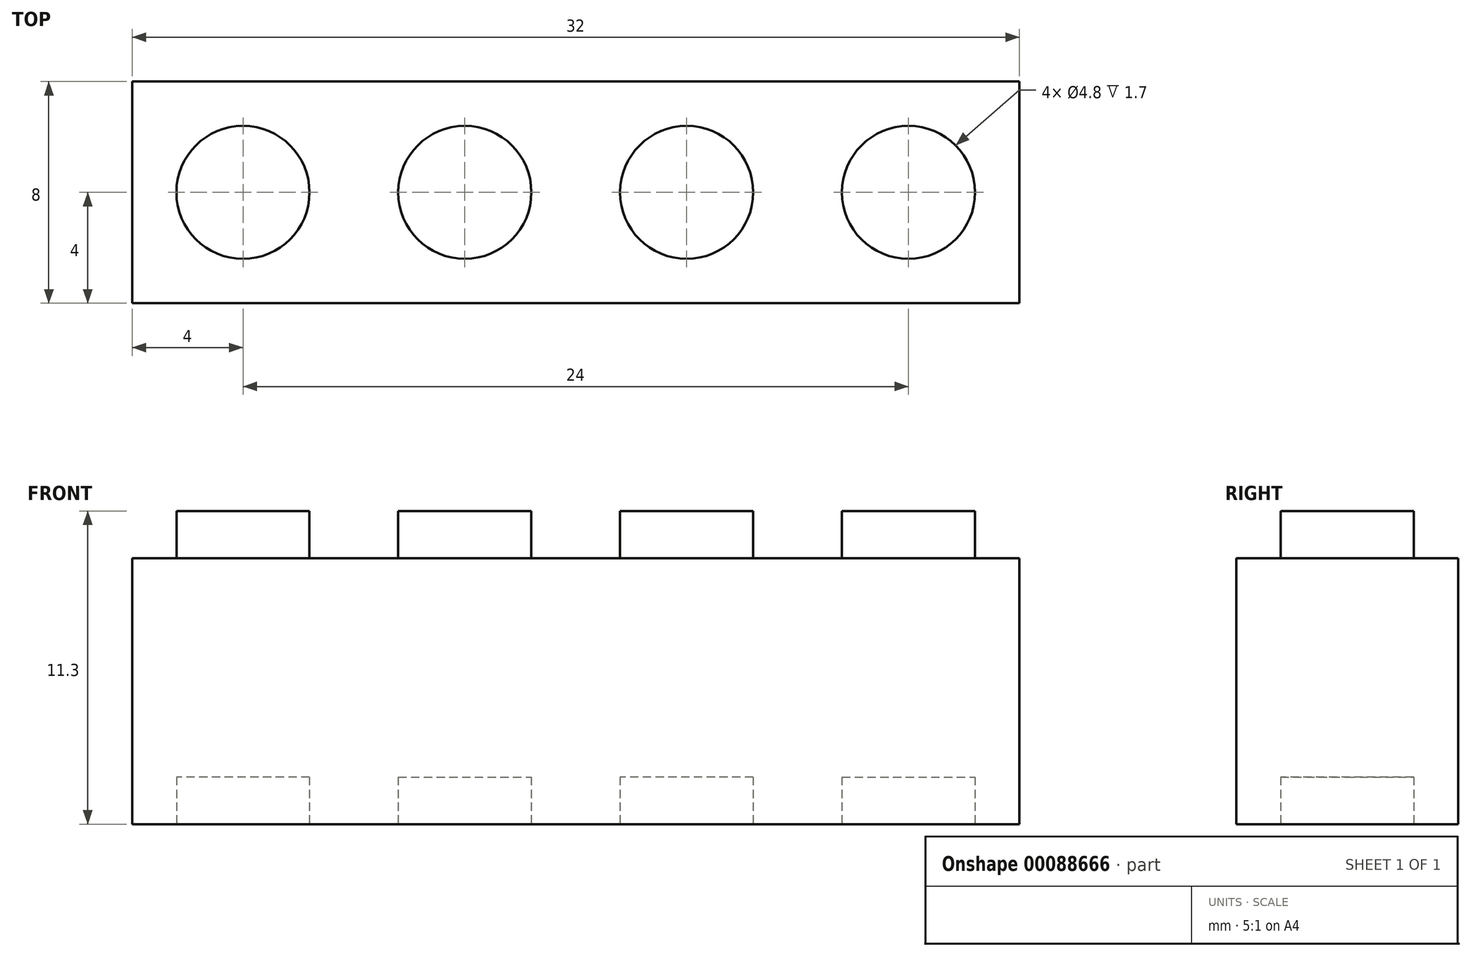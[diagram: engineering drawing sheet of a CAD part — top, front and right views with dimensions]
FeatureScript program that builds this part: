
annotation { "Feature Type Name" : "Feature", "Feature Type Description" : "" }
export const myFeature = defineFeature(function(context is Context, id is Id, definition is map)
    precondition{}
    {
        {
            var Q0;
            Q0=qCreatedBy(makeId("Front.planeOp"),FACE);
            var sketch = newSketch(context, id + "F0", { "sketchPlane" : qUnion([Q0])});
            skLineSegment(sketch, "E0.bottom", {"start": v(-4, 9.6) * mm, "end": v(-2.4, 9.6) * mm});
            skLineSegment(sketch, "E0.top", {"start": v(-4, 0) * mm, "end": v(4, 0) * mm});
            skLineSegment(sketch, "E0.left", {"start": v(-4, 9.6) * mm, "end": v(-4, 0) * mm});
            skLineSegment(sketch, "E0.right", {"start": v(4, 9.6) * mm, "end": v(4, 0) * mm});
            skLineSegment(sketch, "E1.top", {"start": v(-2.4, 11.3) * mm, "end": v(2.4, 11.3) * mm});
            skLineSegment(sketch, "E1.left", {"start": v(-2.4, 9.6) * mm, "end": v(-2.4, 11.3) * mm});
            skLineSegment(sketch, "E1.right", {"start": v(2.4, 9.6) * mm, "end": v(2.4, 11.3) * mm});
            skLineSegment(sketch, "E2", {"start": v(0, 0) * mm, "end": v(0, 24.04) * mm, "construction": true});
            skLineSegment(sketch, "E3.trimOffspring", {"start": v(2.4, 9.6) * mm, "end": v(4, 9.6) * mm});
            skSolve(sketch);
        }
        {
            var Q0;
            Q0=makeQuery(id+"F0.imprint","IMPRINT",FACE,{"disambiguationData":[TD([[makeQuery(id+"F0.imprint","IMPRINT",EDGE,{"derivedFrom":sQuery(id+"F0.wireOp",EDGE,"E0.bottom")}),-1.0]])]});
            extrude(context, id + "F1", {"entities" : qUnion([Q0]), "depth" : 8 * mm});
        }
        {
            var Q0;
            Q0=qCreatedBy(makeId("Top.planeOp"),FACE);
            var Q1;
            Q1=makeQuery(id+"F1.opExtrude","CAP_VERTEX",VERTEX,{"disambiguationData":[OSD([sQuery(id+"F0.wireOp",EDGE,"E1.top"),sQuery(id+"F0.wireOp",EDGE,"E1.right")])],"isStart":true});
            cPlane(context, id + "F2", {"entities" : qUnion([Q0, Q1]), "cplaneType" : CPlaneType.PLANE_POINT, "offset" : 152.4 * mm, "width" : 152.4 * mm, "height" : 152.4 * mm});
        }
        {
            var Q0;
            Q0=qCreatedBy(id+"F2.planeOp",FACE);
            var sketch = newSketch(context, id + "F3", { "sketchPlane" : qUnion([Q0])});
            skLineSegment(sketch, "E4.0", {"start": v(-4, -8) * mm, "end": v(-4, 0) * mm});
            skLineSegment(sketch, "E5.0", {"start": v(4, -8) * mm, "end": v(4, 0) * mm});
            skLineSegment(sketch, "E6", {"start": v(-4, 0) * mm, "end": v(4, 0) * mm});
            skLineSegment(sketch, "E7", {"start": v(-4, -8) * mm, "end": v(4, -8) * mm});
            skLineSegment(sketch, "E8", {"start": v(-4, 0) * mm, "end": v(4, -8) * mm, "construction": true});
            skLineSegment(sketch, "E9", {"start": v(-4, -8) * mm, "end": v(4, 0) * mm, "construction": true});
            skCircle(sketch, "E10", {"center": v(0, -4) * mm, "radius": 2.4 * mm});
            skSolve(sketch);
        }
        {
            var Q0;
            Q0=qSketchRegion(id+"F3",true);
            var Q1;
            Q1=makeQuery(id+"F1.opExtrude","SWEPT_FACE",FACE,{"disambiguationData":[OSD([sQuery(id+"F0.wireOp",EDGE,"E0.bottom")])]});
            extrude(context, id + "F4", {"entities" : qUnion([Q0]), "operationType" : NewBodyOperationType.REMOVE, "endBound" : BoundingType.UP_TO_SURFACE, "oppositeDirection" : true, "endBoundEntityFace" : qUnion([Q1]), "depth" : 25.4 * mm});
        }
        {
            var Q0;
            Q0=qCreatedBy(makeId("Top.planeOp"),FACE);
            var sketch = newSketch(context, id + "F5", { "sketchPlane" : qUnion([Q0])});
            skCircle(sketch, "E11.0", {"center": v(0, -4) * mm, "radius": 2.4 * mm});
            skSolve(sketch);
        }
        {
            var Q0;
            Q0=makeQuery(id+"F5.imprint","IMPRINT",FACE,{"disambiguationData":[TD([[makeQuery(id+"F5.imprint","IMPRINT",EDGE,{"derivedFrom":sQuery(id+"F5.wireOp",EDGE,"E11.0")}),1.0]])]});
            extrude(context, id + "F6", {"entities" : qUnion([Q0]), "operationType" : NewBodyOperationType.REMOVE, "depth" : 1.7 * mm});
        }
        {
            var Q0;
            Q0=qCreatedBy(makeId("Right.planeOp"),FACE);
            var Q1;
            Q1=makeQuery(id+"F1.opExtrude","CAP_VERTEX",VERTEX,{"disambiguationData":[OSD([sQuery(id+"F0.wireOp",EDGE,"E0.right"),sQuery(id+"F0.wireOp",EDGE,"E3.trimOffspring")])],"isStart":false});
            cPlane(context, id + "F7", {"entities" : qUnion([Q0, Q1]), "cplaneType" : CPlaneType.PLANE_POINT, "offset" : 152.4 * mm, "width" : 152.4 * mm, "height" : 152.4 * mm});
        }
        {
            var Q0;
            Q0=makeQuery(id+"F1.opExtrude","SWEPT_BODY",BODY,{"disambiguationData":[OSD([sQuery(id+"F0.wireOp",EDGE,"E0.bottom"),sQuery(id+"F0.wireOp",EDGE,"E0.top"),sQuery(id+"F0.wireOp",EDGE,"E0.left"),sQuery(id+"F0.wireOp",EDGE,"E0.right"),sQuery(id+"F0.wireOp",EDGE,"E1.top"),sQuery(id+"F0.wireOp",EDGE,"E1.left"),sQuery(id+"F0.wireOp",EDGE,"E1.right"),sQuery(id+"F0.wireOp",EDGE,"E3.trimOffspring")])]});
            var Q1;
            Q1=qCreatedBy(id+"F7.planeOp",FACE);
            mirror(context, id + "F8", {"operationType" : NewBodyOperationType.ADD, "entities" : qUnion([Q0]), "mirrorPlane" : qUnion([Q1])});
        }
        {
            var Q0;
            Q0=qCreatedBy(id+"F7.planeOp",FACE);
            var Q1;
            Q1=makeQuery(id+"F8.opPattern","COPY",VERTEX,{"derivedFrom":makeQuery(id+"F1.opExtrude","CAP_VERTEX",VERTEX,{"disambiguationData":[OSD([sQuery(id+"F0.wireOp",EDGE,"E0.bottom"),sQuery(id+"F0.wireOp",EDGE,"E0.left")])],"isStart":false}),"instanceName":"1"});
            cPlane(context, id + "F9", {"entities" : qUnion([Q0, Q1]), "cplaneType" : CPlaneType.PLANE_POINT, "offset" : 152.4 * mm, "width" : 152.4 * mm, "height" : 152.4 * mm});
        }
        {
            var Q0;
            Q0=makeQuery(id+"F1.opExtrude","SWEPT_BODY",BODY,{"disambiguationData":[OSD([sQuery(id+"F0.wireOp",EDGE,"E0.bottom"),sQuery(id+"F0.wireOp",EDGE,"E0.top"),sQuery(id+"F0.wireOp",EDGE,"E0.left"),sQuery(id+"F0.wireOp",EDGE,"E0.right"),sQuery(id+"F0.wireOp",EDGE,"E1.top"),sQuery(id+"F0.wireOp",EDGE,"E1.left"),sQuery(id+"F0.wireOp",EDGE,"E1.right"),sQuery(id+"F0.wireOp",EDGE,"E3.trimOffspring")])]});
            var Q1;
            Q1=qCreatedBy(id+"F9.planeOp",FACE);
            mirror(context, id + "F10", {"operationType" : NewBodyOperationType.ADD, "entities" : qUnion([Q0]), "mirrorPlane" : qUnion([Q1])});
        }
    });
